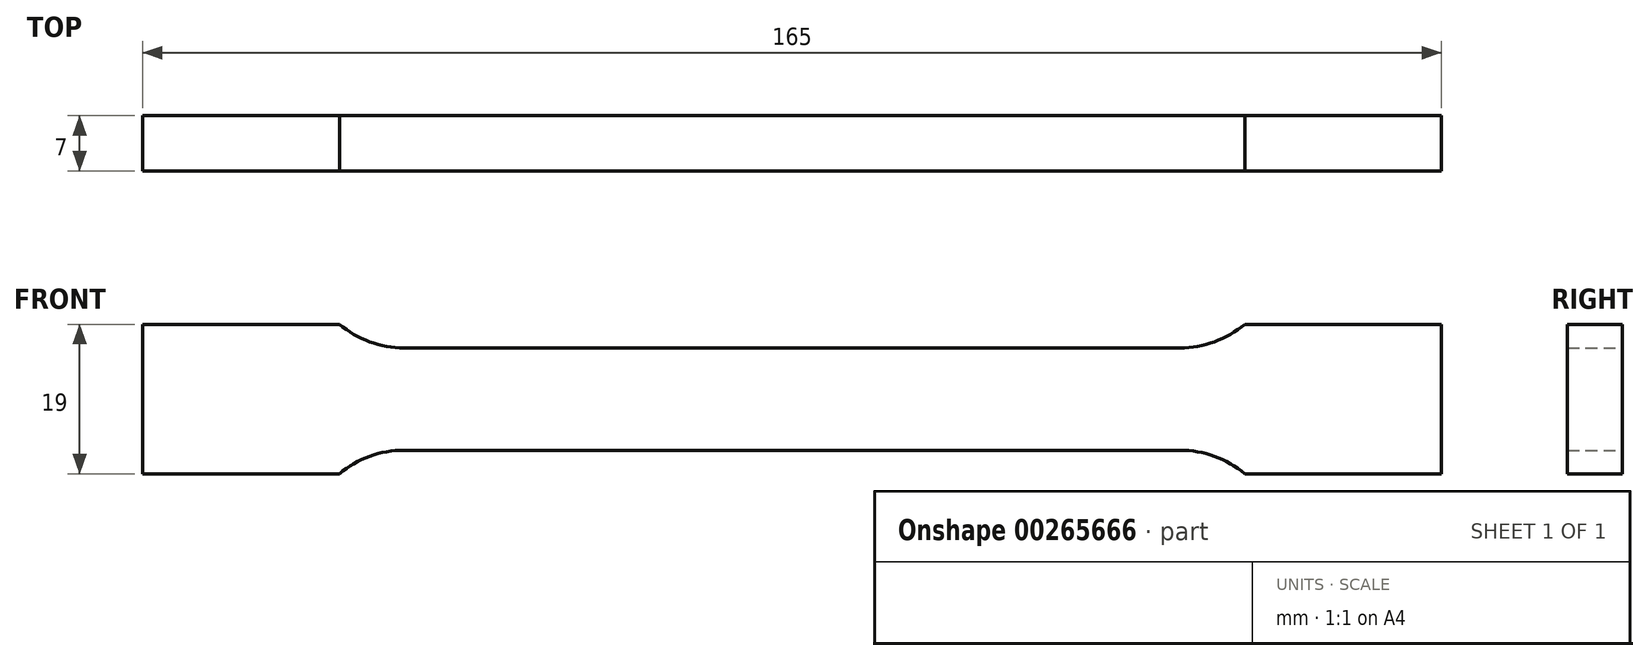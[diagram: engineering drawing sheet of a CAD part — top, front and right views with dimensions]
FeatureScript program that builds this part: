
annotation { "Feature Type Name" : "Feature", "Feature Type Description" : "" }
export const myFeature = defineFeature(function(context is Context, id is Id, definition is map)
    precondition{}
    {
        {
            var Q0;
            Q0=qCreatedBy(makeId("Front.planeOp"),FACE);
            var sketch = newSketch(context, id + "F0", { "sketchPlane" : qUnion([Q0])});
            skLineSegment(sketch, "E0", {"start": v(0, 6.5) * mm, "end": v(49.28, 6.5) * mm});
            skArc(sketch, "E1", {"start": v(49.28, 6.5) * mm, "mid": v(53.65, 7.27) * mm, "end": v(57.5, 9.5) * mm});
            skLineSegment(sketch, "E2", {"start": v(57.5, 9.5) * mm, "end": v(82.5, 9.5) * mm});
            skLineSegment(sketch, "E3", {"start": v(82.5, 9.5) * mm, "end": v(82.5, 0) * mm});
            skLineSegment(sketch, "E4.MirrorCS", {"start": v(0, -6.5) * mm, "end": v(49.28, -6.5) * mm});
            skLineSegment(sketch, "E5.MirrorCS", {"start": v(82.5, -9.5) * mm, "end": v(82.5, 0) * mm});
            skLineSegment(sketch, "E6.MirrorCS", {"start": v(57.5, -9.5) * mm, "end": v(82.5, -9.5) * mm});
            skArc(sketch, "E7.MirrorCS", {"start": v(49.28, -6.5) * mm, "mid": v(53.65, -7.27) * mm, "end": v(57.5, -9.5) * mm});
            skArc(sketch, "E8.MirrorCS", {"start": v(-49.28, -6.5) * mm, "mid": v(-53.65, -7.27) * mm, "end": v(-57.5, -9.5) * mm});
            skLineSegment(sketch, "E9.MirrorCS", {"start": v(-57.5, -9.5) * mm, "end": v(-82.5, -9.5) * mm});
            skArc(sketch, "E10.MirrorCS", {"start": v(-49.28, 6.5) * mm, "mid": v(-53.65, 7.27) * mm, "end": v(-57.5, 9.5) * mm});
            skLineSegment(sketch, "E11.MirrorCS", {"start": v(-57.5, 9.5) * mm, "end": v(-82.5, 9.5) * mm});
            skLineSegment(sketch, "E12.MirrorCS", {"start": v(-82.5, -9.5) * mm, "end": v(-82.5, 0) * mm});
            skLineSegment(sketch, "E13.MirrorCS", {"start": v(0, -6.5) * mm, "end": v(-49.28, -6.5) * mm});
            skLineSegment(sketch, "E14.MirrorCS", {"start": v(-82.5, 9.5) * mm, "end": v(-82.5, 0) * mm});
            skLineSegment(sketch, "E15.MirrorCS", {"start": v(0, 6.5) * mm, "end": v(-49.28, 6.5) * mm});
            skSolve(sketch);
        }
        {
            var Q0;
            Q0 = qSketchRegion(id + "F0", true);
            extrude(context, id + "F1", {"entities" : qUnion([Q0]), "endBound" : BoundingType.SYMMETRIC, "depth" : 7 * mm});
        }
    });
